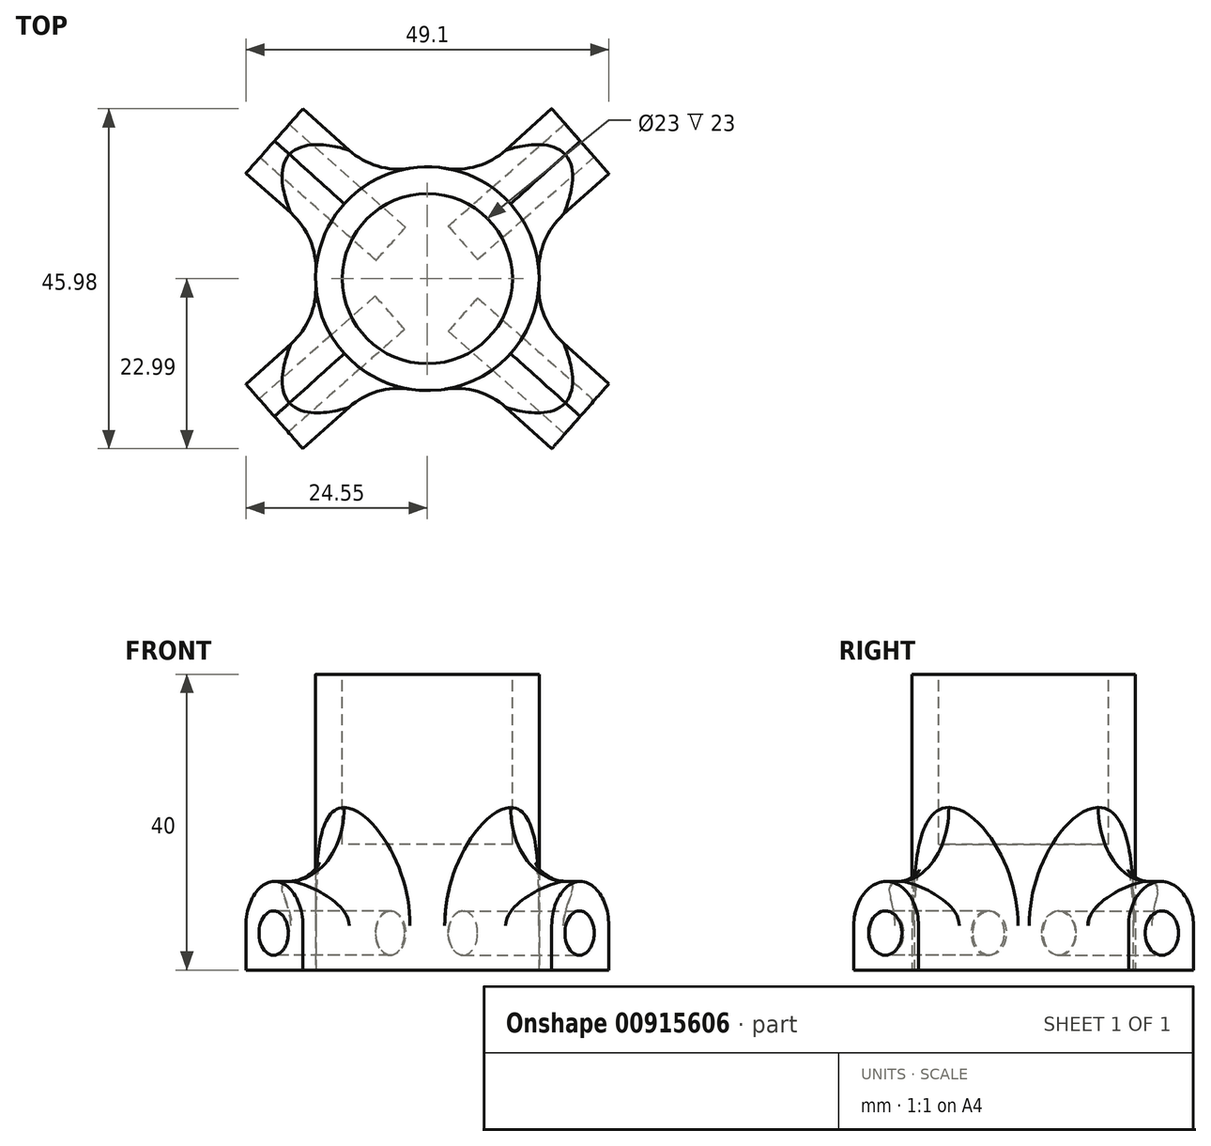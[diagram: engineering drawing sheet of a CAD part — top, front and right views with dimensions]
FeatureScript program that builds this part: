
annotation { "Feature Type Name" : "Feature", "Feature Type Description" : "" }
export const myFeature = defineFeature(function(context is Context, id is Id, definition is map)
    precondition{}
    {
        {
            var Q0;
            Q0=qCreatedBy(makeId("Top.planeOp"),FACE);
            var sketch = newSketch(context, id + "F0", { "sketchPlane" : qUnion([Q0])});
            skPoint(sketch, "E0.middle", {"position": v(23.88, 22.25) * mm});
            skLineSegment(sketch, "E1", {"start": v(48.43, 8.04) * mm, "end": v(40.71, -0.74) * mm});
            skPoint(sketch, "E2.orphan", {"position": v(0, 44.5) * mm});
            skPoint(sketch, "E3.orphan", {"position": v(47.76, 0) * mm});
            skCircle(sketch, "E4", {"center": v(23.88, 22.25) * mm, "radius": 11.12 * mm});
            skCircle(sketch, "E5.0", {"center": v(23.88, 22.25) * mm, "radius": 15.12 * mm});
            skLineSegment(sketch, "E6.0", {"start": v(7.05, -0.74) * mm, "end": v(17.42, 8.57) * mm});
            skLineSegment(sketch, "E7", {"start": v(-0.67, 36.5) * mm, "end": v(7.05, 45.24) * mm});
            skLineSegment(sketch, "E8", {"start": v(7.05, -0.74) * mm, "end": v(-0.67, 8) * mm});
            skLineSegment(sketch, "E9", {"start": v(48.43, 8.04) * mm, "end": v(38.16, 17.27) * mm});
            skLineSegment(sketch, "E10", {"start": v(-0.67, 8) * mm, "end": v(9.6, 17.24) * mm});
            skLineSegment(sketch, "E11", {"start": v(7.05, 45.24) * mm, "end": v(17.41, 35.92) * mm});
            skLineSegment(sketch, "E12", {"start": v(40.71, 45.24) * mm, "end": v(30.35, 35.92) * mm});
            skLineSegment(sketch, "E13", {"start": v(48.43, 36.46) * mm, "end": v(38.16, 27.23) * mm});
            skLineSegment(sketch, "E14", {"start": v(40.71, 45.24) * mm, "end": v(48.43, 36.46) * mm});
            skLineSegment(sketch, "E15", {"start": v(-0.67, 36.5) * mm, "end": v(9.65, 27.39) * mm});
            skPoint(sketch, "E16", {"position": v(30.35, 8.58) * mm});
            skLineSegment(sketch, "E17", {"start": v(40.71, -0.74) * mm, "end": v(30.35, 8.58) * mm});
            skSolve(sketch);
        }
        {
            var Q0;
            Q0 = qSketchRegion(id + "F0", true);
            var Q1;
            Q1=makeQuery(id+"F0.imprint","IMPRINT",FACE,{"disambiguationData":[TD([[makeQuery(id+"F0.imprint","IMPRINT",EDGE,{"derivedFrom":sQuery(id+"F0.wireOp",EDGE,"E4")}),1.0]])]});
            extrude(context, id + "F1", {"entities" : qUnion([Q0, Q1]), "depth" : 12 * mm, "offsetDistance" : 25 * mm});
        }
        {
            var Q0;
            Q0=makeQuery(id+"F0.imprint","IMPRINT",FACE,{"disambiguationData":[TD([[makeQuery(id+"F0.imprint","IMPRINT",EDGE,{"derivedFrom":sQuery(id+"F0.wireOp",EDGE,"E4")}),-1.0]])]});
            extrude(context, id + "F2", {"entities" : qUnion([Q0]), "operationType" : NewBodyOperationType.ADD, "depth" : 40 * mm, "offsetDistance" : 25 * mm});
        }
        {
            var Q0;
            Q0=makeQuery(id+"F0.imprint","IMPRINT",FACE,{"disambiguationData":[TD([[makeQuery(id+"F0.imprint","IMPRINT",EDGE,{"derivedFrom":sQuery(id+"F0.wireOp",EDGE,"E4")}),1.0]])]});
            extrude(context, id + "F3", {"entities" : qUnion([Q0]), "operationType" : NewBodyOperationType.ADD, "depth" : 17 * mm, "offsetDistance" : 25 * mm});
        }
        {
            var Q0;
            Q0=makeQuery(id+"F1.opExtrude","CAP_EDGE",EDGE,{"disambiguationData":[OSD([sQuery(id+"F0.wireOp",EDGE,"E9")])],"isStart":false});
            var Q1;
            Q1=makeQuery(id+"F1.opExtrude","CAP_EDGE",EDGE,{"disambiguationData":[OSD([sQuery(id+"F0.wireOp",EDGE,"E17")])],"isStart":false});
            var Q2;
            Q2=makeQuery(id+"F1.opExtrude","CAP_EDGE",EDGE,{"disambiguationData":[OSD([sQuery(id+"F0.wireOp",EDGE,"E13")])],"isStart":false});
            var Q3;
            Q3=makeQuery(id+"F1.opExtrude","CAP_EDGE",EDGE,{"disambiguationData":[OSD([sQuery(id+"F0.wireOp",EDGE,"E12")])],"isStart":false});
            var Q4;
            Q4=makeQuery(id+"F1.opExtrude","CAP_EDGE",EDGE,{"disambiguationData":[OSD([sQuery(id+"F0.wireOp",EDGE,"E11")])],"isStart":false});
            var Q5;
            Q5=makeQuery(id+"F1.opExtrude","CAP_EDGE",EDGE,{"disambiguationData":[OSD([sQuery(id+"F0.wireOp",EDGE,"E15")])],"isStart":false});
            var Q6;
            Q6=makeQuery(id+"F1.opExtrude","CAP_EDGE",EDGE,{"disambiguationData":[OSD([sQuery(id+"F0.wireOp",EDGE,"E10")])],"isStart":false});
            var Q7;
            Q7=makeQuery(id+"F1.opExtrude","CAP_EDGE",EDGE,{"disambiguationData":[OSD([sQuery(id+"F0.wireOp",EDGE,"E6.0")])],"isStart":false});
            fillet(context, id + "F4", {"entities" : qUnion([Q0, Q1, Q2, Q3, Q4, Q5, Q6, Q7]), "radius" : 6 * mm, "tangentPropagation" : true, "allowEdgeOverflow" : false});
        }
        {
            var Q0;
            Q0=makeQuery(id+"F1.opExtrude","SWEPT_EDGE",EDGE,{"disambiguationData":[OSD([sQuery(id+"F0.wireOp",EDGE,"E5.0"),sQuery(id+"F0.wireOp",EDGE,"E12")])]});
            var Q1;
            Q1=makeQuery(id+"F1.opExtrude","SWEPT_EDGE",EDGE,{"disambiguationData":[OSD([sQuery(id+"F0.wireOp",EDGE,"E5.0"),sQuery(id+"F0.wireOp",EDGE,"E13")])]});
            var Q2;
            Q2=makeQuery(id+"F1.opExtrude","SWEPT_EDGE",EDGE,{"disambiguationData":[OSD([sQuery(id+"F0.wireOp",EDGE,"E5.0"),sQuery(id+"F0.wireOp",EDGE,"E9")])]});
            var Q3;
            Q3=makeQuery(id+"F1.opExtrude","SWEPT_EDGE",EDGE,{"disambiguationData":[OSD([sQuery(id+"F0.wireOp",EDGE,"E5.0"),sQuery(id+"F0.wireOp",EDGE,"E17")])]});
            var Q4;
            Q4=makeQuery(id+"F1.opExtrude","SWEPT_EDGE",EDGE,{"disambiguationData":[OSD([sQuery(id+"F0.wireOp",EDGE,"E5.0"),sQuery(id+"F0.wireOp",EDGE,"E6.0")])]});
            var Q5;
            Q5=makeQuery(id+"F1.opExtrude","SWEPT_EDGE",EDGE,{"disambiguationData":[OSD([sQuery(id+"F0.wireOp",EDGE,"E5.0"),sQuery(id+"F0.wireOp",EDGE,"E10")])]});
            var Q6;
            Q6=makeQuery(id+"F1.opExtrude","SWEPT_EDGE",EDGE,{"disambiguationData":[OSD([sQuery(id+"F0.wireOp",EDGE,"E5.0"),sQuery(id+"F0.wireOp",EDGE,"E15")])]});
            var Q7;
            Q7=makeQuery(id+"F1.opExtrude","SWEPT_EDGE",EDGE,{"disambiguationData":[OSD([sQuery(id+"F0.wireOp",EDGE,"E5.0"),sQuery(id+"F0.wireOp",EDGE,"E11")])]});
            fillet(context, id + "F5", {"entities" : qUnion([Q0, Q1, Q2, Q3, Q4, Q5, Q6, Q7]), "radius" : 10 * mm, "tangentPropagation" : true, "allowEdgeOverflow" : false});
        }
        {
            var Q0;
            Q0=makeQuery(id+"F1.opExtrude","SWEPT_FACE",FACE,{"disambiguationData":[OSD([sQuery(id+"F0.wireOp",EDGE,"E1")])]});
            var sketch = newSketch(context, id + "F6", { "sketchPlane" : qUnion([Q0])});
            skLineSegment(sketch, "E18", {"start": v(26.31, 0) * mm, "end": v(38, 0) * mm});
            skLineSegment(sketch, "E19", {"start": v(32, 0) * mm, "end": v(32, 5) * mm});
            skCircle(sketch, "E20", {"center": v(32, 5) * mm, "radius": 3 * mm});
            skSolve(sketch);
        }
        {
            var Q0;
            Q0=makeQuery(id+"F1.opExtrude","SWEPT_FACE",FACE,{"disambiguationData":[OSD([sQuery(id+"F0.wireOp",EDGE,"E14")])]});
            var sketch = newSketch(context, id + "F7", { "sketchPlane" : qUnion([Q0])});
            skLineSegment(sketch, "E21", {"start": v(-4.58, 0) * mm, "end": v(7.11, 0) * mm});
            skLineSegment(sketch, "E22", {"start": v(1.42, 0) * mm, "end": v(1.42, 5) * mm});
            skCircle(sketch, "E23", {"center": v(1.42, 5) * mm, "radius": 3 * mm});
            skSolve(sketch);
        }
        {
            var Q0;
            Q0=makeQuery(id+"F1.opExtrude","SWEPT_FACE",FACE,{"disambiguationData":[OSD([sQuery(id+"F0.wireOp",EDGE,"E7")])]});
            var sketch = newSketch(context, id + "F8", { "sketchPlane" : qUnion([Q0])});
            skLineSegment(sketch, "E24", {"start": v(-38.58, 0) * mm, "end": v(-26.92, 0) * mm});
            skLineSegment(sketch, "E25", {"start": v(-32.75, 0) * mm, "end": v(-32.75, 5) * mm});
            skCircle(sketch, "E26", {"center": v(-32.75, 5) * mm, "radius": 3 * mm});
            skSolve(sketch);
        }
        {
            var Q0;
            Q0=makeQuery(id+"F1.opExtrude","SWEPT_FACE",FACE,{"disambiguationData":[OSD([sQuery(id+"F0.wireOp",EDGE,"E8")])]});
            var sketch = newSketch(context, id + "F9", { "sketchPlane" : qUnion([Q0])});
            skLineSegment(sketch, "E27", {"start": v(-6.43, 0) * mm, "end": v(5.22, 0) * mm});
            skLineSegment(sketch, "E28", {"start": v(-0.78, 0) * mm, "end": v(-0.78, 5) * mm});
            skCircle(sketch, "E29", {"center": v(-0.78, 5) * mm, "radius": 3 * mm});
            skSolve(sketch);
        }
        {
            var Q0;
            Q0=makeQuery(id+"F9.imprint","IMPRINT",FACE,{"disambiguationData":[TD([[makeQuery(id+"F9.imprint","IMPRINT",EDGE,{"derivedFrom":sQuery(id+"F9.wireOp",EDGE,"E29")}),1.0]])]});
            extrude(context, id + "F10", {"entities" : qUnion([Q0]), "operationType" : NewBodyOperationType.REMOVE, "oppositeDirection" : true, "depth" : 21 * mm, "offsetDistance" : 25 * mm});
        }
        {
            var Q0;
            Q0=makeQuery(id+"F8.imprint","IMPRINT",FACE,{"disambiguationData":[TD([[makeQuery(id+"F8.imprint","IMPRINT",EDGE,{"derivedFrom":sQuery(id+"F8.wireOp",EDGE,"E26")}),1.0]])]});
            extrude(context, id + "F11", {"entities" : qUnion([Q0]), "operationType" : NewBodyOperationType.REMOVE, "oppositeDirection" : true, "depth" : 21 * mm, "offsetDistance" : 25 * mm});
        }
        {
            var Q0;
            Q0=makeQuery(id+"F6.imprint","IMPRINT",FACE,{"disambiguationData":[TD([[makeQuery(id+"F6.imprint","IMPRINT",EDGE,{"derivedFrom":sQuery(id+"F6.wireOp",EDGE,"E20")}),1.0]])]});
            extrude(context, id + "F12", {"entities" : qUnion([Q0]), "operationType" : NewBodyOperationType.REMOVE, "oppositeDirection" : true, "depth" : 21 * mm, "offsetDistance" : 25 * mm});
        }
        {
            var Q0;
            Q0=makeQuery(id+"F7.imprint","IMPRINT",FACE,{"disambiguationData":[TD([[makeQuery(id+"F7.imprint","IMPRINT",EDGE,{"derivedFrom":sQuery(id+"F7.wireOp",EDGE,"E23")}),1.0]])]});
            extrude(context, id + "F13", {"entities" : qUnion([Q0]), "operationType" : NewBodyOperationType.REMOVE, "oppositeDirection" : true, "depth" : 21 * mm, "offsetDistance" : 25 * mm});
        }
        {
            var Q0;
            Q0=makeQuery(id+"F2.opExtrude","CAP_FACE",FACE,{"disambiguationData":[OSD([sQuery(id+"F0.wireOp",EDGE,"E4"),sQuery(id+"F0.wireOp",EDGE,"E5.0")])],"isStart":false});
            var sketch = newSketch(context, id + "F14", { "sketchPlane" : qUnion([Q0])});
            skCircle(sketch, "E30", {"center": v(23.88, 22.25) * mm, "radius": 11.5 * mm});
            skSolve(sketch);
        }
        {
            var Q0;
            Q0=makeQuery(id+"F14.imprint","IMPRINT",FACE,{"disambiguationData":[TD([[makeQuery(id+"F14.imprint","IMPRINT",EDGE,{"derivedFrom":sQuery(id+"F14.wireOp",EDGE,"E30")}),1.0]])]});
            var Q1;
            Q1=makeQuery(id+"F3.opExtrude","CAP_FACE",FACE,{"disambiguationData":[OSD([sQuery(id+"F0.wireOp",EDGE,"E4")])],"isStart":false});
            extrude(context, id + "F15", {"entities" : qUnion([Q0]), "operationType" : NewBodyOperationType.REMOVE, "endBound" : BoundingType.UP_TO_SURFACE, "oppositeDirection" : true, "depth" : 25 * mm, "endBoundEntityFace" : qUnion([Q1]), "offsetDistance" : 25 * mm});
        }
    });
